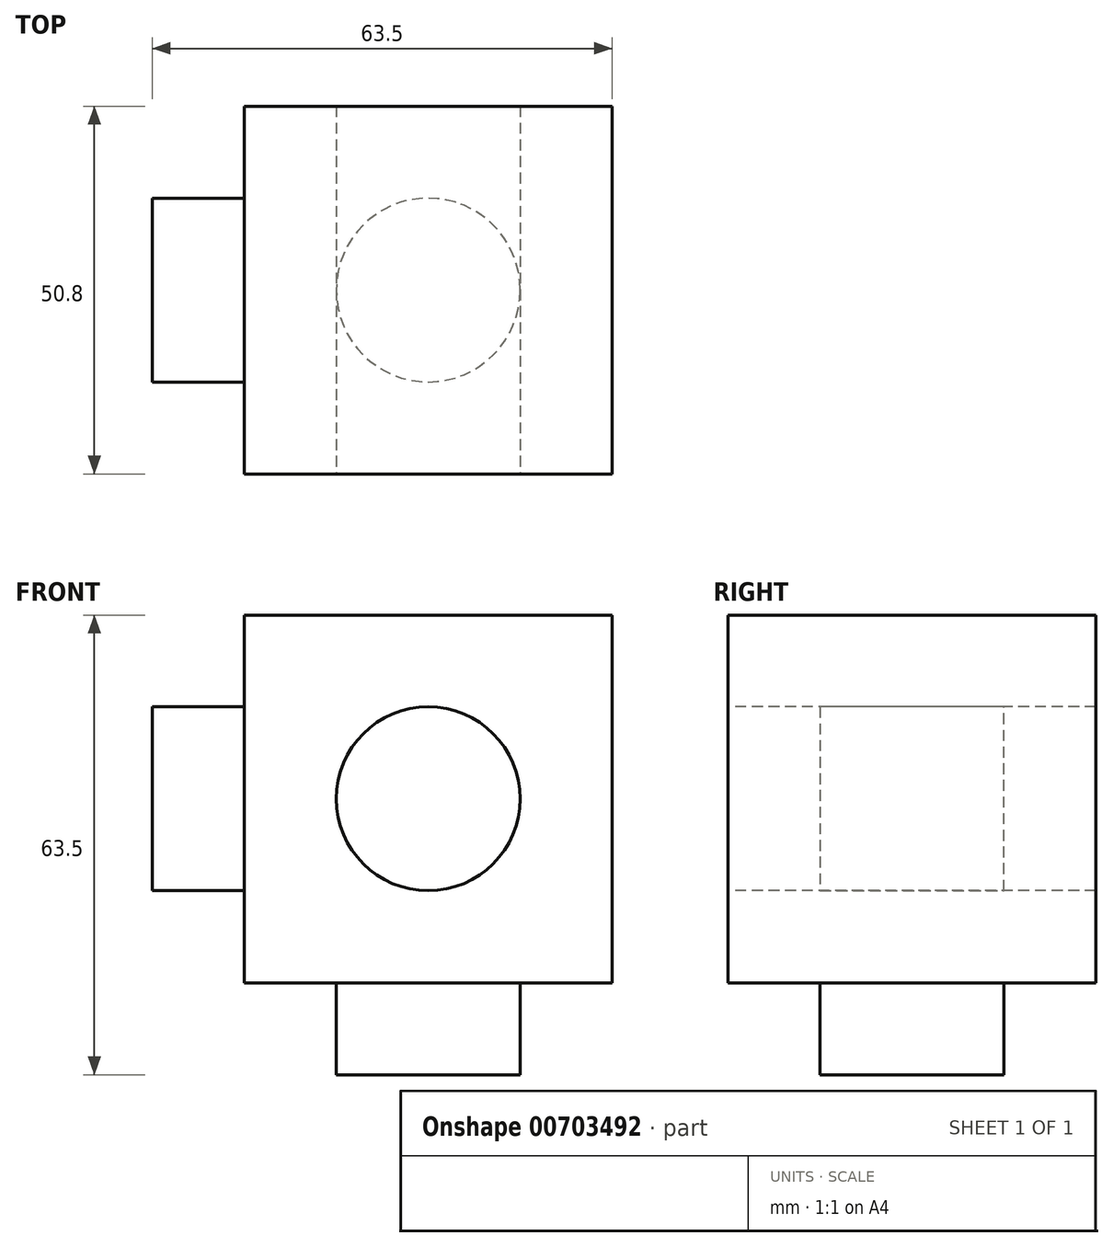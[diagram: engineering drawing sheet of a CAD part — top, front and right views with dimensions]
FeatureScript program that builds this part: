
annotation { "Feature Type Name" : "Feature", "Feature Type Description" : "" }
export const myFeature = defineFeature(function(context is Context, id is Id, definition is map)
    precondition{}
    {
        {
            var Q0;
            Q0=qCreatedBy(makeId("Front.planeOp"),FACE);
            var sketch = newSketch(context, id + "F0", { "sketchPlane" : qUnion([Q0])});
            skLineSegment(sketch, "E0", {"start": v(25.4, 25.38) * mm, "end": v(25.4, -25.42) * mm});
            skLineSegment(sketch, "E1", {"start": v(25.4, -25.42) * mm, "end": v(-25.4, -25.42) * mm});
            skLineSegment(sketch, "E2", {"start": v(-25.4, -25.42) * mm, "end": v(-25.4, 25.38) * mm});
            skPoint(sketch, "E3.end.orphan", {"position": v(0, 25.38) * mm});
            skLineSegment(sketch, "E4", {"start": v(-25.4, 25.38) * mm, "end": v(25.4, 25.38) * mm});
            skPoint(sketch, "E5.start.orphan", {"position": v(-29.82, 0) * mm});
            skPoint(sketch, "E6.end.orphan", {"position": v(-25.4, 0) * mm});
            skPoint(sketch, "E6.start.orphan", {"position": v(25.4, 0) * mm});
            skSolve(sketch);
        }
        {
            var Q0;
            Q0=makeQuery(id+"F0.imprint","IMPRINT",FACE,{"disambiguationData":[TD([[makeQuery(id+"F0.imprint","IMPRINT",EDGE,{"derivedFrom":sQuery(id+"F0.wireOp",EDGE,"E0")}),-1.0]])]});
            extrude(context, id + "F1", {"entities" : qUnion([Q0]), "oppositeDirection" : true, "depth" : 25.4 * mm, "offsetDistance" : 25.4 * mm});
        }
        {
            var Q0;
            Q0 = qSketchRegion(id + "F0", true);
            extrude(context, id + "F2", {"entities" : qUnion([Q0]), "operationType" : NewBodyOperationType.ADD, "depth" : 25.4 * mm, "offsetDistance" : 25.4 * mm});
        }
        {
            var Q0;
            Q0=makeQuery(id+"F2.opExtrude","CAP_FACE",FACE,{"disambiguationData":[OSD([sQuery(id+"F0.wireOp",EDGE,"E0"),sQuery(id+"F0.wireOp",EDGE,"E1"),sQuery(id+"F0.wireOp",EDGE,"E2"),sQuery(id+"F0.wireOp",EDGE,"E4")])],"isStart":false});
            var sketch = newSketch(context, id + "F3", { "sketchPlane" : qUnion([Q0])});
            skCircle(sketch, "E7", {"center": v(0, 0) * mm, "radius": 12.7 * mm});
            skSolve(sketch);
        }
        {
            var Q0;
            Q0 = qSketchRegion(id + "F3", true);
            extrude(context, id + "F4", {"entities" : qUnion([Q0]), "operationType" : NewBodyOperationType.REMOVE, "oppositeDirection" : true, "depth" : 50.8 * mm, "offsetDistance" : 25.4 * mm});
        }
        {
            var Q0;
            {var subQ0=sQuery(id+"F0.wireOp",EDGE,"E1");Q0=makeQuery(id+"F2.boolean.opBoolean","MERGE",FACE,{"derivedFrom":[makeQuery(id+"F1.opExtrude","SWEPT_FACE",FACE,{"disambiguationData":[OSD([subQ0])]}),makeQuery(id+"F2.opExtrude","SWEPT_FACE",FACE,{"disambiguationData":[OSD([subQ0])]})]});}
            var sketch = newSketch(context, id + "F5", { "sketchPlane" : qUnion([Q0])});
            skCircle(sketch, "E8", {"center": v(0, 0) * mm, "radius": 12.7 * mm});
            skSolve(sketch);
        }
        {
            var Q0;
            Q0 = qSketchRegion(id + "F5", true);
            extrude(context, id + "F6", {"entities" : qUnion([Q0]), "operationType" : NewBodyOperationType.ADD, "depth" : 12.7 * mm, "offsetDistance" : 25.4 * mm});
        }
        {
            var Q0;
            {var subQ0=sQuery(id+"F0.wireOp",EDGE,"E2");Q0=makeQuery(id+"F2.boolean.opBoolean","MERGE",FACE,{"derivedFrom":[makeQuery(id+"F1.opExtrude","SWEPT_FACE",FACE,{"disambiguationData":[OSD([subQ0])]}),makeQuery(id+"F2.opExtrude","SWEPT_FACE",FACE,{"disambiguationData":[OSD([subQ0])]})]});}
            var sketch = newSketch(context, id + "F7", { "sketchPlane" : qUnion([Q0])});
            skLineSegment(sketch, "E9", {"start": v(12.7, 12.7) * mm, "end": v(12.7, -12.7) * mm});
            skLineSegment(sketch, "E10", {"start": v(12.7, -12.7) * mm, "end": v(-12.7, -12.7) * mm});
            skLineSegment(sketch, "E11", {"start": v(-12.7, -12.7) * mm, "end": v(-12.7, 12.7) * mm});
            skLineSegment(sketch, "E12", {"start": v(-12.7, 12.7) * mm, "end": v(12.7, 12.7) * mm});
            skSolve(sketch);
        }
        {
            var Q0;
            Q0=makeQuery(id+"F7.imprint","IMPRINT",FACE,{"disambiguationData":[TD([[makeQuery(id+"F7.imprint","IMPRINT",EDGE,{"derivedFrom":sQuery(id+"F7.wireOp",EDGE,"E9")}),-1.0]])]});
            extrude(context, id + "F8", {"entities" : qUnion([Q0]), "operationType" : NewBodyOperationType.ADD, "depth" : 12.7 * mm, "offsetDistance" : 25.4 * mm});
        }
    });
